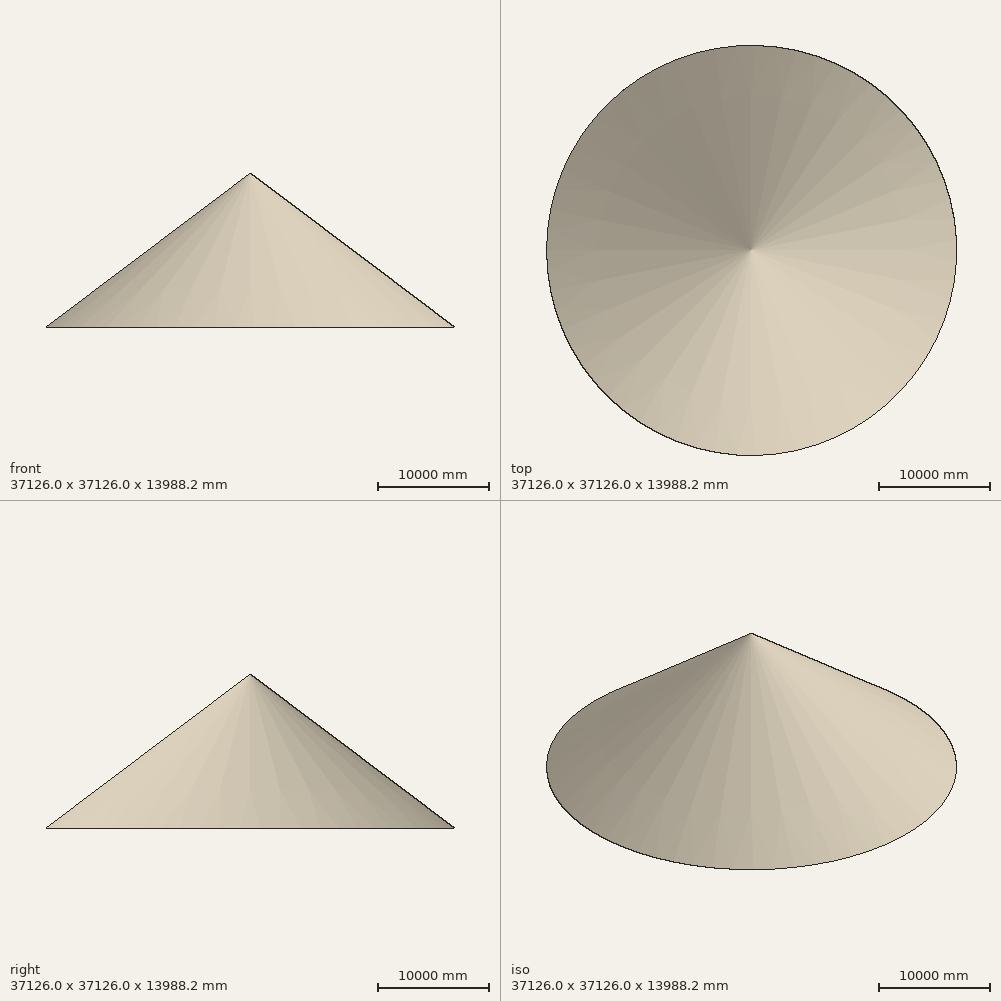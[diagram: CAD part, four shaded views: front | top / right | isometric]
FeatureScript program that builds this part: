
annotation { "Feature Type Name" : "Feature", "Feature Type Description" : "" }
export const myFeature = defineFeature(function(context is Context, id is Id, definition is map)
    precondition{}
    {
        {
            var Q0;
            Q0=qCreatedBy(makeId("Front.planeOp"),FACE);
            var sketch = newSketch(context, id + "F0", { "sketchPlane" : qUnion([Q0])});
            skLineSegment(sketch, "E0", {"start": v(0, 0) * mm, "end": v(0, 13988.22) * mm});
            skLineSegment(sketch, "E1", {"start": v(0, 13988.22) * mm, "end": v(-18563, 0) * mm});
            skLineSegment(sketch, "E2", {"start": v(-18563, 0) * mm, "end": v(0, 0) * mm});
            skSolve(sketch);
        }
        {
            var Q0;
            Q0=makeQuery(id+"F0.imprint","IMPRINT",FACE,{"disambiguationData":[TD([[makeQuery(id+"F0.imprint","IMPRINT",EDGE,{"derivedFrom":sQuery(id+"F0.wireOp",EDGE,"E0")}),1.0]])]});
            var Q1;
            Q1=sQuery(id+"F0.wireOp",EDGE,"E0");
            revolve(context, id + "F1", {"surfaceOperationType" : NewSurfaceOperationType.NEW, "entities" : qUnion([Q0]), "axis" : qUnion([Q1]), "revolveType" : RevolveType.FULL});
        }
    });
